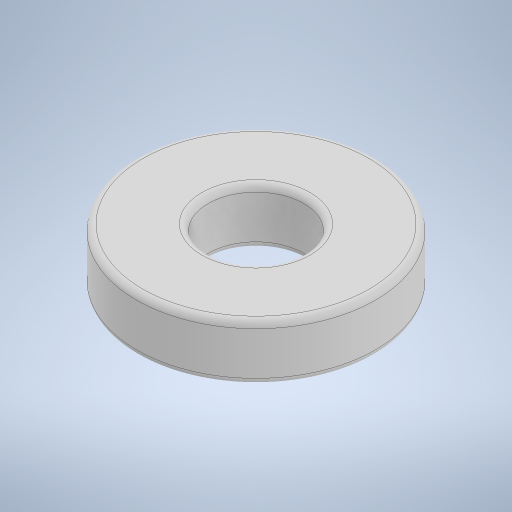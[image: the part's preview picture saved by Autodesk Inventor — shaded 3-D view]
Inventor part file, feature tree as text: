
AUTODESK INVENTOR PART (.ipt)
format: ipt  version: 2024 (Build 280153000, 153)  size: 252,416 bytes
history: native  units: mm
features: extrude x1, fillet x1, sketch x1
ambient origin geometry x8: Origin, YZ Plane, XZ Plane, XY Plane, X Axis, Y Axis, Z Axis, Center Point
bodies: Solid1 (feature_tree)
feature tree (3):
  extrude  "Extrusion1"  Depth=4.0mm
  fillet  "Fillet1"  Radius=150.0mm
  sketch  "Sketch1"  dims[d0=35.0mm d1=0.0mm d2=4.0mm d3=150.0mm d4=60.0mm]
